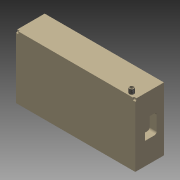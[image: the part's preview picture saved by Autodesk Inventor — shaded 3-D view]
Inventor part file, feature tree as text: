
AUTODESK INVENTOR PART (.ipt)
format: ipt  version: 2015 (Build 190159000, 159)  size: 160,256 bytes
history: native  units: mm
features: extrude x6, sketch x6, fillet x1, pattern_linear x1, shell x1, thread x1, chamfer x1
ambient origin geometry x8: Origin, YZ Plane, XZ Plane, XY Plane, X Axis, Y Axis, Z Axis, Center Point
bodies: 实体1 (feature_tree)
feature tree (17):
  extrude  "拉伸1"  Depth=120.0mm
  extrude  "拉伸2"  Depth=10.0mm
  extrude  "拉伸3"  Depth=10.0mm
  extrude  "拉伸4"  Depth=80.0mm
  fillet  "圆角1"  Radius=30.0mm
  pattern_linear  "矩形阵列1"  Count1=5  [1 undecoded]
  shell  "抽壳1"  Thickness=92.5mm
  extrude  "拉伸5"  Depth=10.0mm
  extrude  "拉伸6"  Depth=5.0mm
  thread  "螺纹1"  [1 undecoded]
  chamfer  "倒角1"  Distance=30.0mm
  sketch  "草图1"  dims[d0=500.0mm d1=120.0mm]
  sketch  "草图2"  dims[d2=265.0mm d3=0.0mm d4=10.0mm]
  sketch  "草图3"  dims[d5=10.0mm d6=0.0mm d7=10.0mm]
  sketch  "草图4"  dims[d8=10.0mm d9=0.0mm d10=80.0mm d11=30.0mm d12=50.0mm d13=92.5mm]
  sketch  "草图5"  dims[d14=30.0mm d15=0.0mm d16=10.0mm]
  sketch  "草图6"  dims[d17=20.0mm d19=470.0mm d20=5.0mm d21=20.0mm d22=30.0mm d23=20.0mm d24=0.0mm d25=15.0mm d26=25.0mm d27=0.0mm d28=10.0mm d29=0.0mm d30=0.5mm d31=2.0mm d32=45.0deg]
note: 2 required parameter values undecoded (feature->parameter linkage not recoverable at this tier; creation-order binding heuristic only, values carry confidence <= 0.55)
